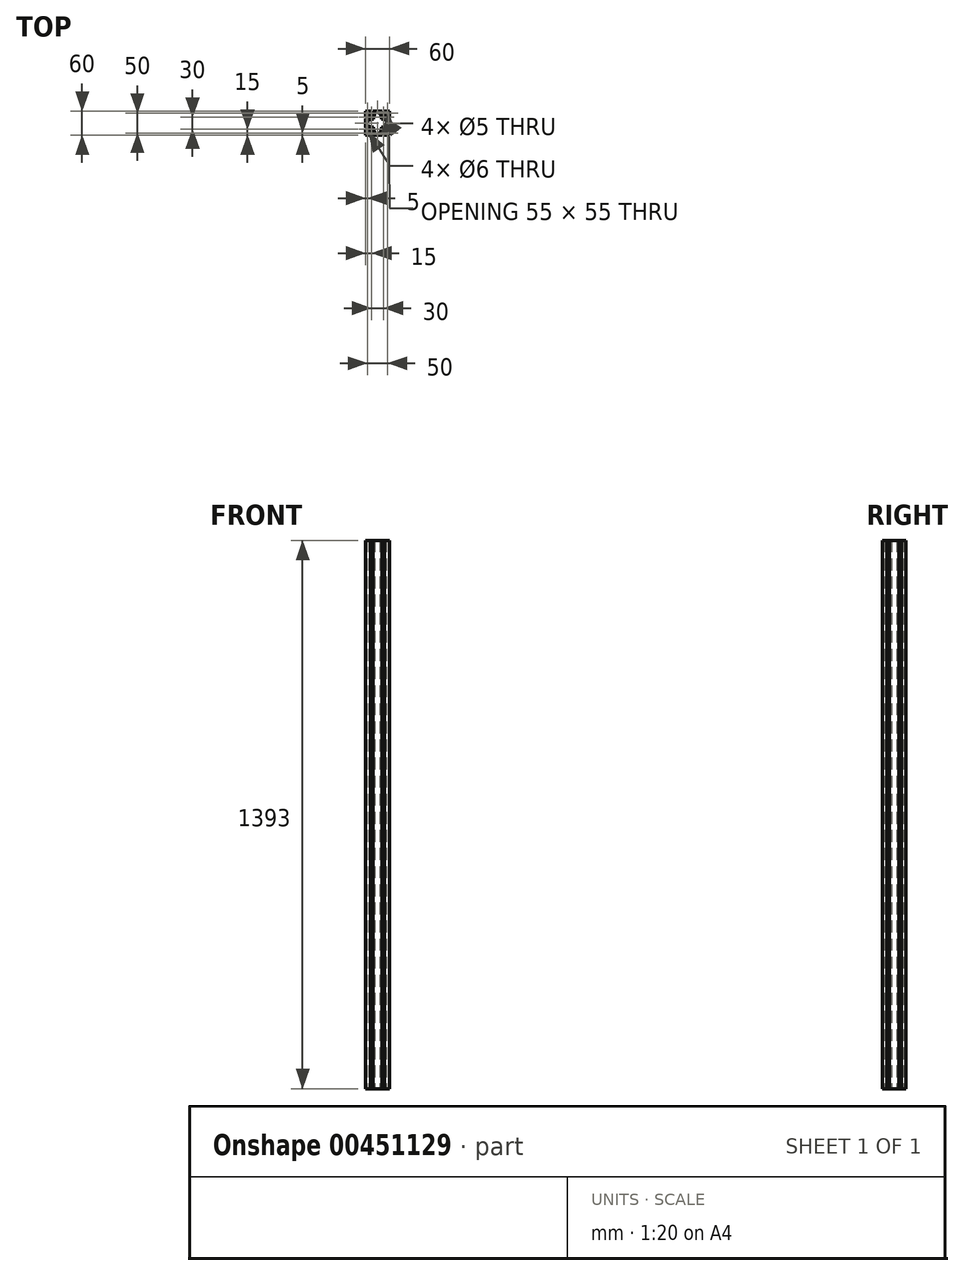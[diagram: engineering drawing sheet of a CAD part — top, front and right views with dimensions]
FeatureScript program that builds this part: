
annotation { "Feature Type Name" : "Feature", "Feature Type Description" : "" }
export const myFeature = defineFeature(function(context is Context, id is Id, definition is map)
    precondition{}
    {
        {
            var Q0;
            Q0=qCreatedBy(makeId("Top.planeOp"),FACE);
            var sketch = newSketch(context, id + "F0", { "sketchPlane" : qUnion([Q0])});
            skLineSegment(sketch, "E0.bottom", {"start": v(30, -30) * mm, "end": v(-30, -30) * mm});
            skLineSegment(sketch, "E0.top", {"start": v(30, 30) * mm, "end": v(-30, 30) * mm});
            skLineSegment(sketch, "E0.left", {"start": v(30, -30) * mm, "end": v(30, 30) * mm});
            skLineSegment(sketch, "E0.right", {"start": v(-30, -30) * mm, "end": v(-30, 30) * mm});
            skPoint(sketch, "E0.middle", {"position": v(0, 0) * mm});
            skLineSegment(sketch, "E1.top", {"start": v(-11.85, 30) * mm, "end": v(-18.15, 30) * mm});
            skLineSegment(sketch, "E1.left", {"start": v(-11.85, 27.5) * mm, "end": v(-11.85, 30) * mm});
            skLineSegment(sketch, "E1.right", {"start": v(-18.15, 27.5) * mm, "end": v(-18.15, 30) * mm});
            skPoint(sketch, "E1.middle", {"position": v(-15, 28.75) * mm});
            skLineSegment(sketch, "E2.bottom", {"start": v(-9.85, 27.5) * mm, "end": v(-11.85, 27.5) * mm});
            skLineSegment(sketch, "E2.left", {"start": v(-9.85, 27.5) * mm, "end": v(-9.85, 21.55) * mm});
            skLineSegment(sketch, "E2.right", {"start": v(-20.15, 27.5) * mm, "end": v(-20.15, 21.55) * mm});
            skPoint(sketch, "E2.middle", {"position": v(-15, 24.52) * mm});
            skArc(sketch, "E3", {"start": v(-20.15, 21.55) * mm, "mid": v(-15, 19.5) * mm, "end": v(-9.85, 21.55) * mm});
            skPoint(sketch, "E4.MirrorP", {"position": v(15, 24.52) * mm});
            skPoint(sketch, "E5.MirrorP", {"position": v(15, 28.75) * mm});
            skLineSegment(sketch, "E6.MirrorCS", {"start": v(11.85, 27.5) * mm, "end": v(11.85, 30) * mm});
            skLineSegment(sketch, "E7.MirrorCS", {"start": v(18.15, 27.5) * mm, "end": v(18.15, 30) * mm});
            skLineSegment(sketch, "E8.MirrorCS", {"start": v(9.85, 27.5) * mm, "end": v(11.85, 27.5) * mm});
            skLineSegment(sketch, "E9.MirrorCS", {"start": v(9.85, 27.5) * mm, "end": v(9.85, 21.55) * mm});
            skArc(sketch, "E10.MirrorCS", {"start": v(20.15, 21.55) * mm, "mid": v(15, 19.5) * mm, "end": v(9.85, 21.55) * mm});
            skLineSegment(sketch, "E11.MirrorCS", {"start": v(20.15, 27.5) * mm, "end": v(20.15, 21.55) * mm});
            skLineSegment(sketch, "E12.MirrorCS", {"start": v(11.85, 30) * mm, "end": v(18.15, 30) * mm});
            skLineSegment(sketch, "E13.1.0", {"start": v(27.5, 20.15) * mm, "end": v(21.55, 20.15) * mm});
            skLineSegment(sketch, "E13.1.1", {"start": v(27.5, 9.85) * mm, "end": v(21.55, 9.85) * mm});
            skArc(sketch, "E13.1.2", {"start": v(21.55, 20.15) * mm, "mid": v(19.5, 15) * mm, "end": v(21.55, 9.85) * mm});
            skLineSegment(sketch, "E13.1.3", {"start": v(27.5, -9.85) * mm, "end": v(21.55, -9.85) * mm});
            skLineSegment(sketch, "E13.1.4", {"start": v(27.5, -20.15) * mm, "end": v(21.55, -20.15) * mm});
            skPoint(sketch, "E13.1.5", {"position": v(28.75, 15) * mm});
            skPoint(sketch, "E13.1.6", {"position": v(28.75, -15) * mm});
            skArc(sketch, "E13.1.7", {"start": v(21.55, -20.15) * mm, "mid": v(19.5, -15) * mm, "end": v(21.55, -9.85) * mm});
            skPoint(sketch, "E13.1.8", {"position": v(24.52, -15) * mm});
            skPoint(sketch, "E13.1.9", {"position": v(24.52, 15) * mm});
            skLineSegment(sketch, "E13.1.10", {"start": v(27.5, 9.85) * mm, "end": v(27.5, 20.15) * mm});
            skLineSegment(sketch, "E13.1.11", {"start": v(27.5, -11.85) * mm, "end": v(27.5, -18.15) * mm});
            skLineSegment(sketch, "E13.1.12", {"start": v(30, 11.85) * mm, "end": v(30, 18.15) * mm});
            skLineSegment(sketch, "E13.1.13", {"start": v(30, -11.85) * mm, "end": v(30, -18.15) * mm});
            skLineSegment(sketch, "E13.1.14", {"start": v(27.5, 18.15) * mm, "end": v(30, 18.15) * mm});
            skLineSegment(sketch, "E13.1.15", {"start": v(27.5, 11.85) * mm, "end": v(30, 11.85) * mm});
            skLineSegment(sketch, "E13.1.16", {"start": v(27.5, 11.85) * mm, "end": v(27.5, 18.15) * mm});
            skLineSegment(sketch, "E13.1.17", {"start": v(27.5, -9.85) * mm, "end": v(27.5, -20.15) * mm});
            skLineSegment(sketch, "E13.1.18", {"start": v(27.5, -18.15) * mm, "end": v(30, -18.15) * mm});
            skLineSegment(sketch, "E13.1.19", {"start": v(27.5, -11.85) * mm, "end": v(30, -11.85) * mm});
            skLineSegment(sketch, "E13.2.0", {"start": v(20.15, -27.5) * mm, "end": v(20.15, -21.55) * mm});
            skLineSegment(sketch, "E13.2.1", {"start": v(9.85, -27.5) * mm, "end": v(9.85, -21.55) * mm});
            skArc(sketch, "E13.2.2", {"start": v(20.15, -21.55) * mm, "mid": v(15, -19.5) * mm, "end": v(9.85, -21.55) * mm});
            skLineSegment(sketch, "E13.2.3", {"start": v(-9.85, -27.5) * mm, "end": v(-9.85, -21.55) * mm});
            skLineSegment(sketch, "E13.2.4", {"start": v(-20.15, -27.5) * mm, "end": v(-20.15, -21.55) * mm});
            skPoint(sketch, "E13.2.5", {"position": v(15, -28.75) * mm});
            skPoint(sketch, "E13.2.6", {"position": v(-15, -28.75) * mm});
            skArc(sketch, "E13.2.7", {"start": v(-20.15, -21.55) * mm, "mid": v(-15, -19.5) * mm, "end": v(-9.85, -21.55) * mm});
            skPoint(sketch, "E13.2.8", {"position": v(-15, -24.52) * mm});
            skPoint(sketch, "E13.2.9", {"position": v(15, -24.52) * mm});
            skLineSegment(sketch, "E13.2.10", {"start": v(9.85, -27.5) * mm, "end": v(20.15, -27.5) * mm});
            skLineSegment(sketch, "E13.2.11", {"start": v(-11.85, -27.5) * mm, "end": v(-18.15, -27.5) * mm});
            skLineSegment(sketch, "E13.2.12", {"start": v(11.85, -30) * mm, "end": v(18.15, -30) * mm});
            skLineSegment(sketch, "E13.2.13", {"start": v(-11.85, -30) * mm, "end": v(-18.15, -30) * mm});
            skLineSegment(sketch, "E13.2.14", {"start": v(18.15, -27.5) * mm, "end": v(18.15, -30) * mm});
            skLineSegment(sketch, "E13.2.15", {"start": v(11.85, -27.5) * mm, "end": v(11.85, -30) * mm});
            skLineSegment(sketch, "E13.2.16", {"start": v(11.85, -27.5) * mm, "end": v(18.15, -27.5) * mm});
            skLineSegment(sketch, "E13.2.17", {"start": v(-9.85, -27.5) * mm, "end": v(-20.15, -27.5) * mm});
            skLineSegment(sketch, "E13.2.18", {"start": v(-18.15, -27.5) * mm, "end": v(-18.15, -30) * mm});
            skLineSegment(sketch, "E13.2.19", {"start": v(-11.85, -27.5) * mm, "end": v(-11.85, -30) * mm});
            skLineSegment(sketch, "E13.3.0", {"start": v(-27.5, -20.15) * mm, "end": v(-21.55, -20.15) * mm});
            skLineSegment(sketch, "E13.3.1", {"start": v(-27.5, -9.85) * mm, "end": v(-21.55, -9.85) * mm});
            skArc(sketch, "E13.3.2", {"start": v(-21.55, -20.15) * mm, "mid": v(-19.5, -15) * mm, "end": v(-21.55, -9.85) * mm});
            skLineSegment(sketch, "E13.3.3", {"start": v(-27.5, 9.85) * mm, "end": v(-21.55, 9.85) * mm});
            skLineSegment(sketch, "E13.3.4", {"start": v(-27.5, 20.15) * mm, "end": v(-21.55, 20.15) * mm});
            skPoint(sketch, "E13.3.5", {"position": v(-28.75, -15) * mm});
            skPoint(sketch, "E13.3.6", {"position": v(-28.75, 15) * mm});
            skArc(sketch, "E13.3.7", {"start": v(-21.55, 20.15) * mm, "mid": v(-19.5, 15) * mm, "end": v(-21.55, 9.85) * mm});
            skPoint(sketch, "E13.3.8", {"position": v(-24.52, 15) * mm});
            skPoint(sketch, "E13.3.9", {"position": v(-24.52, -15) * mm});
            skLineSegment(sketch, "E13.3.10", {"start": v(-27.5, -9.85) * mm, "end": v(-27.5, -20.15) * mm});
            skLineSegment(sketch, "E13.3.11", {"start": v(-27.5, 11.85) * mm, "end": v(-27.5, 18.15) * mm});
            skLineSegment(sketch, "E13.3.12", {"start": v(-30, -11.85) * mm, "end": v(-30, -18.15) * mm});
            skLineSegment(sketch, "E13.3.13", {"start": v(-30, 11.85) * mm, "end": v(-30, 18.15) * mm});
            skLineSegment(sketch, "E13.3.14", {"start": v(-27.5, -18.15) * mm, "end": v(-30, -18.15) * mm});
            skLineSegment(sketch, "E13.3.15", {"start": v(-27.5, -11.85) * mm, "end": v(-30, -11.85) * mm});
            skLineSegment(sketch, "E13.3.16", {"start": v(-27.5, -11.85) * mm, "end": v(-27.5, -18.15) * mm});
            skLineSegment(sketch, "E13.3.17", {"start": v(-27.5, 9.85) * mm, "end": v(-27.5, 20.15) * mm});
            skLineSegment(sketch, "E13.3.18", {"start": v(-27.5, 18.15) * mm, "end": v(-30, 18.15) * mm});
            skLineSegment(sketch, "E13.3.19", {"start": v(-27.5, 11.85) * mm, "end": v(-30, 11.85) * mm});
            skLineSegment(sketch, "E13.anchor1", {"start": v(0, 0) * mm, "end": v(-20.15, 21.55) * mm, "construction": true});
            skLineSegment(sketch, "E13.anchor2", {"start": v(0, 0) * mm, "end": v(-21.55, -20.15) * mm, "construction": true});
            skLineSegment(sketch, "E14.trimOffspring", {"start": v(-18.15, 27.5) * mm, "end": v(-20.15, 27.5) * mm});
            skLineSegment(sketch, "E15.trimOffspring", {"start": v(18.15, 27.5) * mm, "end": v(20.15, 27.5) * mm});
            skCircle(sketch, "E16", {"center": v(-15, 15) * mm, "radius": 2.5 * mm});
            skCircle(sketch, "E17", {"center": v(-25, 25) * mm, "radius": 3 * mm});
            skCircle(sketch, "E18.MirrorC", {"center": v(25, 25) * mm, "radius": 3 * mm});
            skCircle(sketch, "E19.MirrorC", {"center": v(25, -25) * mm, "radius": 3 * mm});
            skCircle(sketch, "E20.MirrorC", {"center": v(-25, -25) * mm, "radius": 3 * mm});
            skCircle(sketch, "E21.MirrorC", {"center": v(15, 15) * mm, "radius": 2.5 * mm});
            skCircle(sketch, "E22.MirrorC", {"center": v(15, -15) * mm, "radius": 2.5 * mm});
            skCircle(sketch, "E23.MirrorC", {"center": v(-15, -15) * mm, "radius": 2.5 * mm});
            skLineSegment(sketch, "E24", {"start": v(-7, 27.5) * mm, "end": v(0, 27.5) * mm});
            skLineSegment(sketch, "E25", {"start": v(-7, 27.5) * mm, "end": v(-7, 22) * mm});
            skLineSegment(sketch, "E26", {"start": v(-10, 10) * mm, "end": v(-10, 16) * mm});
            skLineSegment(sketch, "E27", {"start": v(-10, 16) * mm, "end": v(-7, 22) * mm});
            skLineSegment(sketch, "E28.MirrorCS", {"start": v(10, 10) * mm, "end": v(10, 16) * mm});
            skLineSegment(sketch, "E29.MirrorCS", {"start": v(10, 16) * mm, "end": v(7, 22) * mm});
            skLineSegment(sketch, "E30.MirrorCS", {"start": v(7, 27.5) * mm, "end": v(0, 27.5) * mm});
            skLineSegment(sketch, "E31.MirrorCS", {"start": v(7, 27.5) * mm, "end": v(7, 22) * mm});
            skLineSegment(sketch, "E32.1.0", {"start": v(-10, -10) * mm, "end": v(-16, -10) * mm});
            skLineSegment(sketch, "E32.1.1", {"start": v(-16, -10) * mm, "end": v(-22, -7) * mm});
            skLineSegment(sketch, "E32.1.2", {"start": v(-27.5, -7) * mm, "end": v(-22, -7) * mm});
            skLineSegment(sketch, "E32.1.3", {"start": v(-27.5, -7) * mm, "end": v(-27.5, 0) * mm});
            skLineSegment(sketch, "E32.1.4", {"start": v(-27.5, 7) * mm, "end": v(-27.5, 0) * mm});
            skLineSegment(sketch, "E32.1.5", {"start": v(-27.5, 7) * mm, "end": v(-22, 7) * mm});
            skLineSegment(sketch, "E32.1.6", {"start": v(-16, 10) * mm, "end": v(-22, 7) * mm});
            skLineSegment(sketch, "E32.1.7", {"start": v(-10, 10) * mm, "end": v(-16, 10) * mm});
            skLineSegment(sketch, "E32.2.0", {"start": v(10, -10) * mm, "end": v(10, -16) * mm});
            skLineSegment(sketch, "E32.2.1", {"start": v(10, -16) * mm, "end": v(7, -22) * mm});
            skLineSegment(sketch, "E32.2.2", {"start": v(7, -27.5) * mm, "end": v(7, -22) * mm});
            skLineSegment(sketch, "E32.2.3", {"start": v(7, -27.5) * mm, "end": v(0, -27.5) * mm});
            skLineSegment(sketch, "E32.2.4", {"start": v(-7, -27.5) * mm, "end": v(0, -27.5) * mm});
            skLineSegment(sketch, "E32.2.5", {"start": v(-7, -27.5) * mm, "end": v(-7, -22) * mm});
            skLineSegment(sketch, "E32.2.6", {"start": v(-10, -16) * mm, "end": v(-7, -22) * mm});
            skLineSegment(sketch, "E32.2.7", {"start": v(-10, -10) * mm, "end": v(-10, -16) * mm});
            skLineSegment(sketch, "E32.3.0", {"start": v(10, 10) * mm, "end": v(16, 10) * mm});
            skLineSegment(sketch, "E32.3.1", {"start": v(16, 10) * mm, "end": v(22, 7) * mm});
            skLineSegment(sketch, "E32.3.2", {"start": v(27.5, 7) * mm, "end": v(22, 7) * mm});
            skLineSegment(sketch, "E32.3.3", {"start": v(27.5, 7) * mm, "end": v(27.5, 0) * mm});
            skLineSegment(sketch, "E32.3.4", {"start": v(27.5, -7) * mm, "end": v(27.5, 0) * mm});
            skLineSegment(sketch, "E32.3.5", {"start": v(27.5, -7) * mm, "end": v(22, -7) * mm});
            skLineSegment(sketch, "E32.3.6", {"start": v(16, -10) * mm, "end": v(22, -7) * mm});
            skLineSegment(sketch, "E32.3.7", {"start": v(10, -10) * mm, "end": v(16, -10) * mm});
            skSolve(sketch);
        }
        {
            var Q0;
            {var subQ30=sQuery(id+"F0.wireOp",EDGE,"E1.left");Q0=makeQuery(id+"F0.imprint","IMPRINT",FACE,{"disambiguationData":[TD([[makeQuery(id+"F0.imprint","IMPRINT",EDGE,{"derivedFrom":subQ30}),-1.0]])]});}
            extrude(context, id + "F1", {"entities" : qUnion([Q0]), "depth" : 1393 * mm, "offsetDistance" : 25 * mm});
        }
        {
            var Q0;
            Q0=makeQuery(id+"F1.opExtrude","SWEPT_EDGE",EDGE,{"disambiguationData":[OSD([sQuery(id+"F0.wireOp",EDGE,"E24"),sQuery(id+"F0.wireOp",EDGE,"E25")])]});
            var Q1;
            Q1=makeQuery(id+"F1.opExtrude","SWEPT_EDGE",EDGE,{"disambiguationData":[OSD([sQuery(id+"F0.wireOp",EDGE,"E30.MirrorCS"),sQuery(id+"F0.wireOp",EDGE,"E31.MirrorCS")])]});
            var Q2;
            Q2=makeQuery(id+"F1.opExtrude","SWEPT_EDGE",EDGE,{"disambiguationData":[OSD([sQuery(id+"F0.wireOp",EDGE,"840db5bc-c403-45cd-90c7-254e62d9e8c5.3.2"),sQuery(id+"F0.wireOp",EDGE,"840db5bc-c403-45cd-90c7-254e62d9e8c5.3.3")])]});
            var Q3;
            Q3=makeQuery(id+"F1.opExtrude","SWEPT_EDGE",EDGE,{"disambiguationData":[OSD([sQuery(id+"F0.wireOp",EDGE,"840db5bc-c403-45cd-90c7-254e62d9e8c5.3.4"),sQuery(id+"F0.wireOp",EDGE,"840db5bc-c403-45cd-90c7-254e62d9e8c5.3.5")])]});
            var Q4;
            Q4=makeQuery(id+"F1.opExtrude","SWEPT_EDGE",EDGE,{"disambiguationData":[OSD([sQuery(id+"F0.wireOp",EDGE,"840db5bc-c403-45cd-90c7-254e62d9e8c5.1.4"),sQuery(id+"F0.wireOp",EDGE,"840db5bc-c403-45cd-90c7-254e62d9e8c5.1.5")])]});
            var Q5;
            Q5=makeQuery(id+"F1.opExtrude","SWEPT_EDGE",EDGE,{"disambiguationData":[OSD([sQuery(id+"F0.wireOp",EDGE,"840db5bc-c403-45cd-90c7-254e62d9e8c5.1.2"),sQuery(id+"F0.wireOp",EDGE,"840db5bc-c403-45cd-90c7-254e62d9e8c5.1.3")])]});
            var Q6;
            Q6=makeQuery(id+"F1.opExtrude","SWEPT_EDGE",EDGE,{"disambiguationData":[OSD([sQuery(id+"F0.wireOp",EDGE,"840db5bc-c403-45cd-90c7-254e62d9e8c5.2.2"),sQuery(id+"F0.wireOp",EDGE,"840db5bc-c403-45cd-90c7-254e62d9e8c5.2.3")])]});
            var Q7;
            Q7=makeQuery(id+"F1.opExtrude","SWEPT_EDGE",EDGE,{"disambiguationData":[OSD([sQuery(id+"F0.wireOp",EDGE,"840db5bc-c403-45cd-90c7-254e62d9e8c5.2.4"),sQuery(id+"F0.wireOp",EDGE,"840db5bc-c403-45cd-90c7-254e62d9e8c5.2.5")])]});
            fillet(context, id + "F2", {"entities" : qUnion([Q0, Q1, Q2, Q3, Q4, Q5, Q6, Q7]), "radius" : 2 * mm, "tangentPropagation" : true, "allowEdgeOverflow" : false});
        }
        {
            var Q0;
            Q0=makeQuery(id+"F1.opExtrude","SWEPT_EDGE",EDGE,{"disambiguationData":[OSD([sQuery(id+"F0.wireOp",EDGE,"E26"),sQuery(id+"F0.wireOp",EDGE,"E27")])]});
            var Q1;
            Q1=makeQuery(id+"F1.opExtrude","SWEPT_EDGE",EDGE,{"disambiguationData":[OSD([sQuery(id+"F0.wireOp",EDGE,"E28.MirrorCS"),sQuery(id+"F0.wireOp",EDGE,"E29.MirrorCS")])]});
            var Q2;
            Q2=makeQuery(id+"F1.opExtrude","SWEPT_EDGE",EDGE,{"disambiguationData":[OSD([sQuery(id+"F0.wireOp",EDGE,"840db5bc-c403-45cd-90c7-254e62d9e8c5.3.0"),sQuery(id+"F0.wireOp",EDGE,"840db5bc-c403-45cd-90c7-254e62d9e8c5.3.1")])]});
            var Q3;
            Q3=makeQuery(id+"F1.opExtrude","SWEPT_EDGE",EDGE,{"disambiguationData":[OSD([sQuery(id+"F0.wireOp",EDGE,"840db5bc-c403-45cd-90c7-254e62d9e8c5.1.6"),sQuery(id+"F0.wireOp",EDGE,"840db5bc-c403-45cd-90c7-254e62d9e8c5.1.7")])]});
            var Q4;
            Q4=makeQuery(id+"F1.opExtrude","SWEPT_EDGE",EDGE,{"disambiguationData":[OSD([sQuery(id+"F0.wireOp",EDGE,"840db5bc-c403-45cd-90c7-254e62d9e8c5.1.0"),sQuery(id+"F0.wireOp",EDGE,"840db5bc-c403-45cd-90c7-254e62d9e8c5.1.1")])]});
            var Q5;
            Q5=makeQuery(id+"F1.opExtrude","SWEPT_EDGE",EDGE,{"disambiguationData":[OSD([sQuery(id+"F0.wireOp",EDGE,"840db5bc-c403-45cd-90c7-254e62d9e8c5.3.6"),sQuery(id+"F0.wireOp",EDGE,"840db5bc-c403-45cd-90c7-254e62d9e8c5.3.7")])]});
            var Q6;
            Q6=makeQuery(id+"F1.opExtrude","SWEPT_EDGE",EDGE,{"disambiguationData":[OSD([sQuery(id+"F0.wireOp",EDGE,"840db5bc-c403-45cd-90c7-254e62d9e8c5.2.0"),sQuery(id+"F0.wireOp",EDGE,"840db5bc-c403-45cd-90c7-254e62d9e8c5.2.1")])]});
            var Q7;
            Q7=makeQuery(id+"F1.opExtrude","SWEPT_EDGE",EDGE,{"disambiguationData":[OSD([sQuery(id+"F0.wireOp",EDGE,"840db5bc-c403-45cd-90c7-254e62d9e8c5.2.6"),sQuery(id+"F0.wireOp",EDGE,"840db5bc-c403-45cd-90c7-254e62d9e8c5.2.7")])]});
            fillet(context, id + "F3", {"entities" : qUnion([Q0, Q1, Q2, Q3, Q4, Q5, Q6, Q7]), "radius" : 7 * mm, "tangentPropagation" : true, "allowEdgeOverflow" : false});
        }
    });
